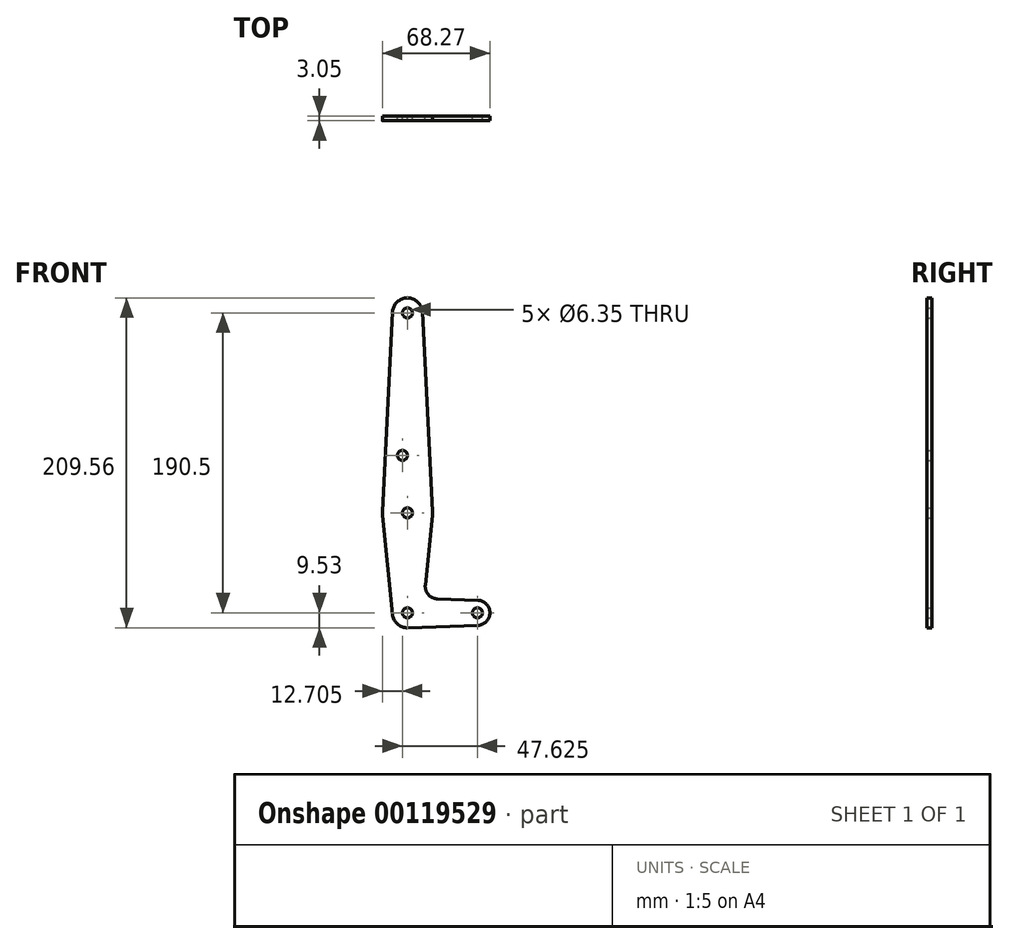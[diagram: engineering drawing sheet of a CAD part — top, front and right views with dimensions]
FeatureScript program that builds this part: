
annotation { "Feature Type Name" : "Feature", "Feature Type Description" : "" }
export const myFeature = defineFeature(function(context is Context, id is Id, definition is map)
    precondition{}
    {
        {
            var Q0;
            Q0=qCreatedBy(makeId("Front.planeOp"),FACE);
            var sketch = newSketch(context, id + "F0", { "sketchPlane" : qUnion([Q0])});
            skCircle(sketch, "E0", {"center": v(0, 0) * mm, "radius": 15.88 * mm});
            skCircle(sketch, "E1", {"center": v(0, 127) * mm, "radius": 9.53 * mm});
            skCircle(sketch, "E2", {"center": v(0, -63.5) * mm, "radius": 9.53 * mm});
            skCircle(sketch, "E3", {"center": v(44.45, -63.5) * mm, "radius": 7.94 * mm});
            skLineSegment(sketch, "E4", {"start": v(0, -63.5) * mm, "end": v(44.45, -63.5) * mm, "construction": true});
            skLineSegment(sketch, "E5", {"start": v(0, 127) * mm, "end": v(0, -63.5) * mm, "construction": true});
            skLineSegment(sketch, "E6", {"start": v(-9.51, 127.48) * mm, "end": v(-15.86, 0.8) * mm});
            skLineSegment(sketch, "E7", {"start": v(-15.8, -1.59) * mm, "end": v(-9.48, -64.45) * mm});
            skLineSegment(sketch, "E8", {"start": v(9.51, 127.48) * mm, "end": v(15.86, 0.8) * mm});
            skLineSegment(sketch, "E9", {"start": v(15.8, -1.59) * mm, "end": v(11.34, -45.9) * mm});
            skLineSegment(sketch, "E10", {"start": v(18.97, -54.65) * mm, "end": v(44.73, -55.57) * mm});
            skLineSegment(sketch, "E11", {"start": v(0.34, -73.02) * mm, "end": v(44.73, -71.43) * mm});
            skCircle(sketch, "E12", {"center": v(0, 127) * mm, "radius": 3.18 * mm});
            skCircle(sketch, "E13", {"center": v(-3.17, 36.53) * mm, "radius": 3.18 * mm});
            skCircle(sketch, "E14", {"center": v(0, 0) * mm, "radius": 3.18 * mm});
            skCircle(sketch, "E15", {"center": v(0, -63.5) * mm, "radius": 3.18 * mm});
            skCircle(sketch, "E16", {"center": v(44.45, -63.5) * mm, "radius": 3.18 * mm});
            skLineSegment(sketch, "E17", {"start": v(0, 0) * mm, "end": v(-42.47, 0) * mm, "construction": true});
            skArc(sketch, "E18.filletArc", {"start": v(11.34, -45.9) * mm, "mid": v(13.26, -51.93) * mm, "end": v(18.97, -54.65) * mm});
            skSolve(sketch);
        }
        {
            var Q0;
            Q0=makeQuery(id+"F0.imprint","IMPRINT",FACE,{"disambiguationData":[TD([[makeQuery(id+"F0.imprint","IMPRINT",EDGE,{"derivedFrom":sQuery(id+"F0.wireOp",EDGE,"E12")}),-1.0]])]});
            var Q1;
            Q1=makeQuery(id+"F0.imprint","IMPRINT",FACE,{"disambiguationData":[TD([[makeQuery(id+"F0.imprint","IMPRINT",EDGE,{"derivedFrom":sQuery(id+"F0.wireOp",EDGE,"E14")}),-1.0]])]});
            var Q2;
            {var subQ0=sQuery(id+"F0.wireOp",EDGE,"E7");Q2=makeQuery(id+"F0.imprint","IMPRINT",FACE,{"disambiguationData":[TD([[makeQuery(id+"F0.imprint","IMPRINT",EDGE,{"derivedFrom":subQ0}),1.0]])]});}
            var Q3;
            {var subQ1=sQuery(id+"F0.wireOp",EDGE,"E6");Q3=makeQuery(id+"F0.imprint","IMPRINT",FACE,{"disambiguationData":[TD([[makeQuery(id+"F0.imprint","IMPRINT",EDGE,{"derivedFrom":subQ1}),1.0]])]});}
            var Q4;
            Q4=makeQuery(id+"F0.imprint","IMPRINT",FACE,{"disambiguationData":[TD([[makeQuery(id+"F0.imprint","IMPRINT",EDGE,{"derivedFrom":sQuery(id+"F0.wireOp",EDGE,"E15")}),-1.0]])]});
            var Q5;
            Q5=makeQuery(id+"F0.imprint","IMPRINT",FACE,{"disambiguationData":[TD([[makeQuery(id+"F0.imprint","IMPRINT",EDGE,{"derivedFrom":sQuery(id+"F0.wireOp",EDGE,"E16")}),-1.0]])]});
            extrude(context, id + "F1", {"entities" : qUnion([Q0, Q1, Q2, Q3, Q4, Q5]), "depth" : 3.05 * mm});
        }
    });
